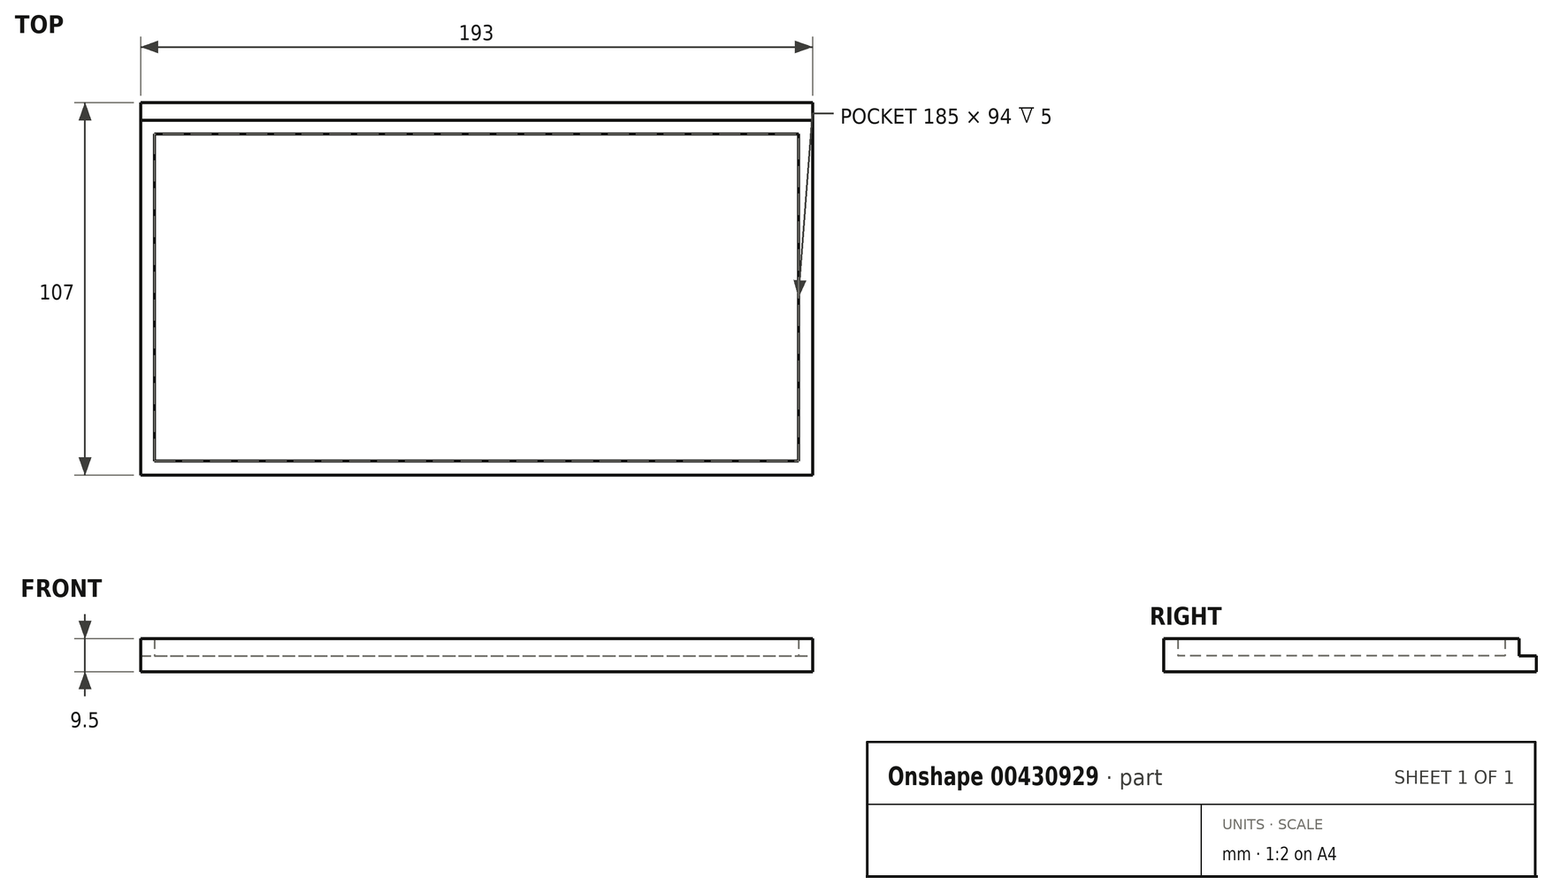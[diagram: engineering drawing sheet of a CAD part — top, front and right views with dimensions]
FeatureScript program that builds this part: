
annotation { "Feature Type Name" : "Feature", "Feature Type Description" : "" }
export const myFeature = defineFeature(function(context is Context, id is Id, definition is map)
    precondition{}
    {
        {
            var Q0;
            Q0=qCreatedBy(makeId("Top.planeOp"),FACE);
            var sketch = newSketch(context, id + "F0", { "sketchPlane" : qUnion([Q0])});
            skLineSegment(sketch, "E0.left", {"start": v(96.5, 61) * mm, "end": v(96.5, -56) * mm});
            skLineSegment(sketch, "E0.right", {"start": v(-96.5, 56) * mm, "end": v(-96.5, -56) * mm});
            skPoint(sketch, "E0.middle", {"position": v(0, 0) * mm});
            skLineSegment(sketch, "E1.top", {"start": v(-96.5, -46) * mm, "end": v(96.5, -46) * mm});
            skLineSegment(sketch, "E1.left", {"start": v(-96.5, -56) * mm, "end": v(-96.5, -46) * mm});
            skLineSegment(sketch, "E1.right", {"start": v(96.5, -56) * mm, "end": v(96.5, -46) * mm});
            skLineSegment(sketch, "E2.top", {"start": v(-92.5, -42) * mm, "end": v(92.5, -42) * mm});
            skLineSegment(sketch, "E2.left", {"start": v(-96.5, -46) * mm, "end": v(-96.5, -42) * mm});
            skLineSegment(sketch, "E2.right", {"start": v(96.5, -46) * mm, "end": v(96.5, -42) * mm});
            skLineSegment(sketch, "E3.top", {"start": v(-96.5, 56) * mm, "end": v(96.5, 56) * mm});
            skLineSegment(sketch, "E3.left", {"start": v(-96.5, 61) * mm, "end": v(-96.5, 56) * mm});
            skLineSegment(sketch, "E3.right", {"start": v(96.5, 61) * mm, "end": v(96.5, 56) * mm});
            skLineSegment(sketch, "E4.top", {"start": v(-92.5, 52) * mm, "end": v(92.5, 52) * mm});
            skLineSegment(sketch, "E4.left", {"start": v(-96.5, 56) * mm, "end": v(-96.5, 52) * mm});
            skLineSegment(sketch, "E4.right", {"start": v(96.5, 56) * mm, "end": v(96.5, 52) * mm});
            skLineSegment(sketch, "E5.left", {"start": v(-96.5, 52) * mm, "end": v(-96.5, -42) * mm});
            skLineSegment(sketch, "E5.right", {"start": v(-92.5, 52) * mm, "end": v(-92.5, -42) * mm});
            skLineSegment(sketch, "E6.left", {"start": v(96.5, 52) * mm, "end": v(96.5, -42) * mm});
            skLineSegment(sketch, "E6.right", {"start": v(92.5, 52) * mm, "end": v(92.5, -42) * mm});
            skLineSegment(sketch, "E7.top", {"start": v(-96.5, 61) * mm, "end": v(96.5, 61) * mm});
            skPoint(sketch, "E8.orphan", {"position": v(-96.5, 63) * mm});
            skPoint(sketch, "E9.orphan", {"position": v(96.5, 63) * mm});
            skPoint(sketch, "E10.orphan", {"position": v(-96.5, -63) * mm});
            skPoint(sketch, "E11.orphan", {"position": v(96.5, -63) * mm});
            skLineSegment(sketch, "E12.top", {"start": v(-96.5, -56) * mm, "end": v(96.5, -56) * mm});
            skSolve(sketch);
        }
        {
            var Q0;
            Q0=makeQuery(id+"F0.imprint","IMPRINT",FACE,{"disambiguationData":[TD([[makeQuery(id+"F0.imprint","IMPRINT",EDGE,{"derivedFrom":sQuery(id+"F0.wireOp",EDGE,"E3.bottom")}),-1.0]])]});
            var Q1;
            Q1=makeQuery(id+"F0.imprint","IMPRINT",FACE,{"disambiguationData":[TD([[makeQuery(id+"F0.imprint","IMPRINT",EDGE,{"derivedFrom":sQuery(id+"F0.wireOp",EDGE,"E1.top")}),1.0]])]});
            var Q2;
            Q2=makeQuery(id+"F0.imprint","IMPRINT",FACE,{"disambiguationData":[TD([[makeQuery(id+"F0.imprint","IMPRINT",EDGE,{"derivedFrom":sQuery(id+"F0.wireOp",EDGE,"E2.top")}),1.0]])]});
            var Q3;
            Q3=makeQuery(id+"F0.imprint","IMPRINT",FACE,{"disambiguationData":[TD([[makeQuery(id+"F0.imprint","IMPRINT",EDGE,{"derivedFrom":sQuery(id+"F0.wireOp",EDGE,"E1.bottom")}),1.0]])]});
            var Q4;
            Q4=makeQuery(id+"F0.imprint","IMPRINT",FACE,{"disambiguationData":[TD([[makeQuery(id+"F0.imprint","IMPRINT",EDGE,{"derivedFrom":sQuery(id+"F0.wireOp",EDGE,"E1.left")}),-1.0]])]});
            var Q5;
            Q5=makeQuery(id+"F0.imprint","IMPRINT",FACE,{"disambiguationData":[TD([[makeQuery(id+"F0.imprint","IMPRINT",EDGE,{"derivedFrom":sQuery(id+"F0.wireOp",EDGE,"E3.left")}),1.0]])]});
            extrude(context, id + "F1", {"entities" : qUnion([Q0, Q1, Q2, Q3, Q4, Q5]), "oppositeDirection" : true, "depth" : 4.5 * mm});
        }
        {
            var Q0;
            Q0=makeQuery(id+"F0.imprint","IMPRINT",FACE,{"disambiguationData":[TD([[makeQuery(id+"F0.imprint","IMPRINT",EDGE,{"derivedFrom":sQuery(id+"F0.wireOp",EDGE,"E1.top")}),1.0]])]});
            extrude(context, id + "F2", {"entities" : qUnion([Q0]), "operationType" : NewBodyOperationType.ADD, "depth" : 5 * mm});
        }
    });
